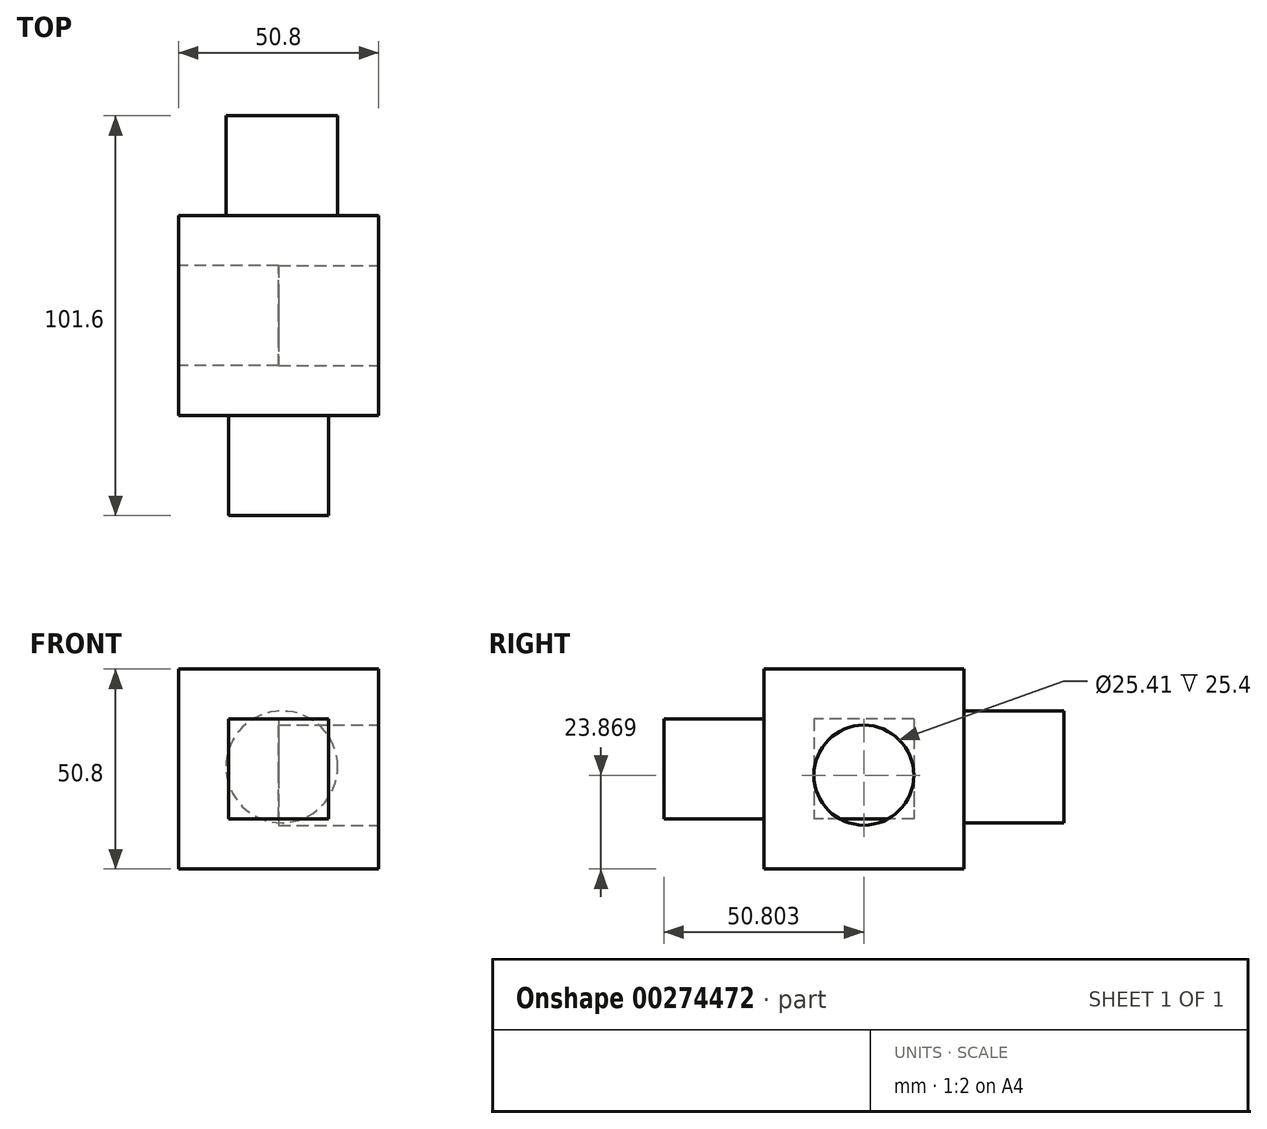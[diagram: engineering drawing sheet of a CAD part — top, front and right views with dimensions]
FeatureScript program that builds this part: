
annotation { "Feature Type Name" : "Feature", "Feature Type Description" : "" }
export const myFeature = defineFeature(function(context is Context, id is Id, definition is map)
    precondition{}
    {
        {
            var Q0;
            Q0=qCreatedBy(makeId("Front.planeOp"),FACE);
            var sketch = newSketch(context, id + "F0", { "sketchPlane" : qUnion([Q0])});
            skLineSegment(sketch, "E0", {"start": v(0, 0) * mm, "end": v(0, 50.8) * mm});
            skLineSegment(sketch, "E1", {"start": v(0, 50.8) * mm, "end": v(-50.8, 50.8) * mm});
            skLineSegment(sketch, "E2", {"start": v(-50.8, 50.8) * mm, "end": v(-50.8, 0) * mm});
            skLineSegment(sketch, "E3", {"start": v(-50.8, 0) * mm, "end": v(0, 0) * mm});
            skSolve(sketch);
        }
        {
            var Q0;
            Q0 = qSketchRegion(id + "F0", true);
            extrude(context, id + "F1", {"entities" : qUnion([Q0]), "depth" : 50.8 * mm});
        }
        {
            var Q0;
            Q0=makeQuery(id+"F1.opExtrude","CAP_FACE",FACE,{"disambiguationData":[OSD([sQuery(id+"F0.wireOp",EDGE,"E0"),sQuery(id+"F0.wireOp",EDGE,"E1"),sQuery(id+"F0.wireOp",EDGE,"E2"),sQuery(id+"F0.wireOp",EDGE,"E3")])],"isStart":false});
            var sketch = newSketch(context, id + "F2", { "sketchPlane" : qUnion([Q0])});
            skLineSegment(sketch, "E4.bottom", {"start": v(-12.7, 12.7) * mm, "end": v(-38.1, 12.7) * mm});
            skLineSegment(sketch, "E4.top", {"start": v(-12.7, 38.1) * mm, "end": v(-38.1, 38.1) * mm});
            skLineSegment(sketch, "E4.left", {"start": v(-12.7, 12.7) * mm, "end": v(-12.7, 38.1) * mm});
            skLineSegment(sketch, "E4.right", {"start": v(-38.1, 12.7) * mm, "end": v(-38.1, 38.1) * mm});
            skSolve(sketch);
        }
        {
            var Q0;
            Q0 = qSketchRegion(id + "F2", true);
            extrude(context, id + "F3", {"entities" : qUnion([Q0]), "operationType" : NewBodyOperationType.ADD, "depth" : 25.4 * mm});
        }
        {
            var Q0;
            Q0=makeQuery(id+"F1.opExtrude","SWEPT_FACE",FACE,{"disambiguationData":[OSD([sQuery(id+"F0.wireOp",EDGE,"E2")])]});
            var sketch = newSketch(context, id + "F4", { "sketchPlane" : qUnion([Q0])});
            skLineSegment(sketch, "E5.bottom", {"start": v(12.7, 38.1) * mm, "end": v(38.1, 38.1) * mm});
            skLineSegment(sketch, "E5.top", {"start": v(12.7, 12.7) * mm, "end": v(38.1, 12.7) * mm});
            skLineSegment(sketch, "E5.left", {"start": v(12.7, 38.1) * mm, "end": v(12.7, 12.7) * mm});
            skLineSegment(sketch, "E5.right", {"start": v(38.1, 38.1) * mm, "end": v(38.1, 12.7) * mm});
            skSolve(sketch);
        }
        {
            var Q0;
            Q0 = qSketchRegion(id + "F4", true);
            extrude(context, id + "F5", {"entities" : qUnion([Q0]), "operationType" : NewBodyOperationType.REMOVE, "oppositeDirection" : true, "depth" : 25.4 * mm});
        }
        {
            var Q0;
            Q0=makeQuery(id+"F1.opExtrude","SWEPT_FACE",FACE,{"disambiguationData":[OSD([sQuery(id+"F0.wireOp",EDGE,"E0")])]});
            var sketch = newSketch(context, id + "F6", { "sketchPlane" : qUnion([Q0])});
            skCircle(sketch, "E6", {"center": v(-25.4, 23.87) * mm, "radius": 12.7 * mm});
            skSolve(sketch);
        }
        {
            var Q0;
            Q0 = qSketchRegion(id + "F6", true);
            extrude(context, id + "F7", {"entities" : qUnion([Q0]), "operationType" : NewBodyOperationType.REMOVE, "oppositeDirection" : true, "depth" : 25.4 * mm});
        }
        {
            var Q0;
            Q0=makeQuery(id+"F1.opExtrude","CAP_FACE",FACE,{"disambiguationData":[OSD([sQuery(id+"F0.wireOp",EDGE,"E0"),sQuery(id+"F0.wireOp",EDGE,"E1"),sQuery(id+"F0.wireOp",EDGE,"E2"),sQuery(id+"F0.wireOp",EDGE,"E3")])],"isStart":true});
            var sketch = newSketch(context, id + "F8", { "sketchPlane" : qUnion([Q0])});
            skCircle(sketch, "E7", {"center": v(24.57, 25.97) * mm, "radius": 14.2 * mm});
            skSolve(sketch);
        }
        {
            var Q0;
            Q0 = qSketchRegion(id + "F8", true);
            extrude(context, id + "F9", {"entities" : qUnion([Q0]), "operationType" : NewBodyOperationType.ADD, "depth" : 25.4 * mm});
        }
    });
